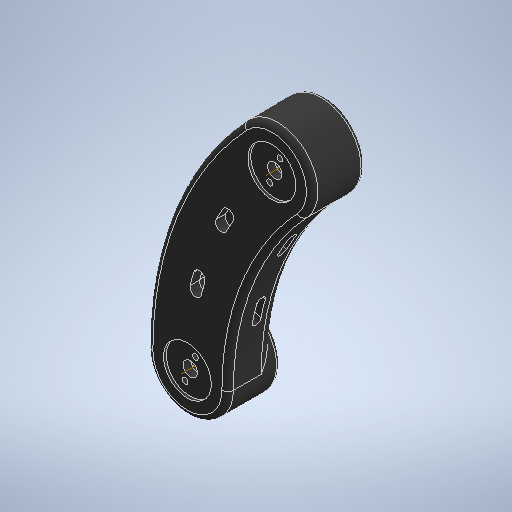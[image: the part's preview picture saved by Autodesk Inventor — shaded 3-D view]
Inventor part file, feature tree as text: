
AUTODESK INVENTOR PART (.ipt)
format: ipt  version: 2025.2 (Build 292293000, 293)  size: 564,736 bytes
history: native  units: mm
features: sketch x9, extrude x8, projected_geometry x4, fillet x3, revolve x2, plane x2, other x2, shell x1, chamfer x1
ambient origin geometry x8: Origin, YZ Plane, XZ Plane, XY Plane, X Axis, Y Axis, Z Axis, Center Point
bodies: Solid1 (feature_tree)
feature tree (32):
  sketch  "Sketch2"  dims[d26=42.0mm d51=27.5mm d52=0.0mm d53=25.0mm d54=1.5mm d55=0.0mm]
  extrude  "Extrusion6"  Depth=27.5mm TaperAngle=0.0deg
  shell  "Shell1"  Thickness=25.0mm
  chamfer  "Chamfer1"  Distance=1.5mm
  extrude  "Extrusion9"  Depth=14.5mm
  extrude  "Extrusion1"  Depth=3.0mm
  extrude  "Extrusion2"  Depth=32.0mm
  extrude  "Extrusion3"  Depth=32.0mm
  extrude  "Extrusion4"  TaperAngle=90.0deg  [1 undecoded]
  revolve  "Revolution1"  [1 undecoded]
  plane  "Work Plane1"
  revolve  "Revolution2"  [1 undecoded]
  extrude  "Extrusion5"  Depth=13.75mm TaperAngle=0.0deg
  plane  "Work Plane2"
  extrude  "Extrusion10"  Depth=2.0mm TaperAngle=0.0deg
  fillet  "Fillet2"  Radius=5.0mm
  fillet  "Fillet3"  Radius=2.0mm
  fillet  "Fillet4"  Radius=6.0mm
  sketch  "Sketch3"  dims[d56=7.5mm d57=14.5mm]
  sketch  "Sketch4"  dims[d58=3.0mm d61=3.759439mm]
  sketch  "Sketch5"  dims[d62=1.5mm d63=0.0mm d64=32.0mm]
  sketch  "Sketch6"  dims[d65=1.0mm d66=0.0mm d67=32.0mm]
  sketch  "Sketch7"  dims[d70=13.0mm d71=90.0deg]
  projected_geometry  "Projected Loop1"
  projected_geometry  "Projected Loop2"
  sketch  "Sketch8"  dims[d73=22.0mm d74=0.0mm d106=3.759439mm]
  projected_geometry  "Projected Loop3"
  sketch  "Sketch13"  dims[d107=44.064mm d108=32.0mm d109=13.0mm]
  projected_geometry  "Projected Loop5"
  other  "Work Axis1"
  other  "Work Axis2"
  sketch  "Sketch14"  dims[d110=90.0deg d112=13.75mm d113=0.0mm d116=10.75mm d117=0.0mm d118=5.0mm d130=5.0mm d131=2.0mm d132=45.0deg d136=6.0mm d141=1.396263mm d142=0.0mm d143=0.0mm d144=0.436332mm d145=0.436332mm d146=239.999923mm d147=3.759971mm d149=10.0mm d151=40.0mm d152=60.0mm d153=0.0mm d154=0.0mm d155=7.0mm d156=3.0mm d157=2.0mm]
note: 3 required parameter values undecoded (feature->parameter linkage not recoverable at this tier; creation-order binding heuristic only, values carry confidence <= 0.55)